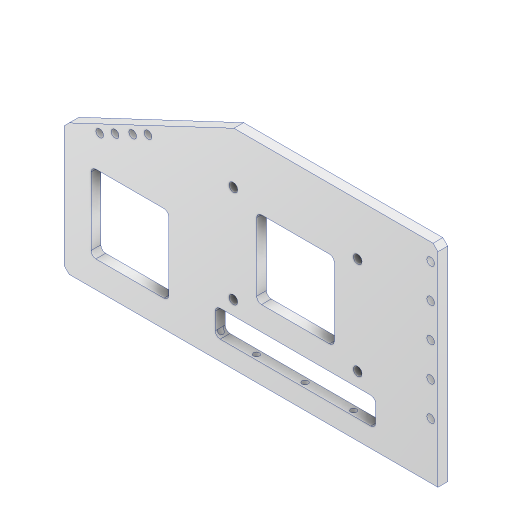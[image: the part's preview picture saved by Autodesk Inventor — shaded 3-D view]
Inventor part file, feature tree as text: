
AUTODESK INVENTOR PART (.ipt)
format: ipt  version: 2023.2 (Build 272271000, 271)  size: 518,656 bytes
history: native  units: mm
features: extrude x12, sketch x12, projected_geometry x9, fillet x3, other x1, chamfer x1
ambient origin geometry x8: Origin, YZ Plane, XZ Plane, XY Plane, X Axis, Y Axis, Z Axis, Center Point
bodies: Body1 (feature_tree)
feature tree (38):
  other  "솔리드1"
  extrude  "돌출1"  Depth=4.0mm TaperAngle=0.0deg
  extrude  "돌출4"  Depth=75.0mm
  extrude  "돌출5"  Depth=32.0mm
  extrude  "돌출6"  Depth=4.0mm TaperAngle=0.0deg
  extrude  "돌출7"  Depth=4.0mm TaperAngle=0.0deg
  fillet  "모깎기1"  Radius=32.0mm
  extrude  "돌출8"  Depth=4.0mm TaperAngle=0.0deg
  extrude  "돌출9"  Depth=5.5mm
  fillet  "모깎기2"  Radius=6.0mm
  chamfer  "모따기1"  Angle=90.0deg  [1 undecoded]
  extrude  "돌출12"  Depth=36.0mm
  extrude  "돌출13"  Depth=3.2mm
  extrude  "돌출14"  Depth=3.2mm
  extrude  "돌출15"  Depth=3.2mm
  fillet  "모깎기3"  Radius=3.2mm
  extrude  "돌출10"  Depth=7.0mm
  sketch  "스케치1"
  sketch  "스케치3"
  projected_geometry  "투영된 루프1"
  sketch  "스케치6"
  projected_geometry  "투영된 루프3"
  sketch  "스케치9"
  projected_geometry  "투영된 루프4"
  sketch  "스케치10"
  sketch  "스케치11"
  projected_geometry  "투영된 루프5"
  sketch  "스케치12"
  projected_geometry  "투영된 루프6"
  sketch  "스케치13"
  sketch  "스케치15"
  projected_geometry  "투영된 루프8"
  sketch  "스케치16"
  projected_geometry  "투영된 루프9"
  sketch  "스케치17"
  projected_geometry  "투영된 루프10"
  sketch  "스케치18"
  projected_geometry  "투영된 루프11"
note: 1 required parameter value undecoded (feature->parameter linkage not recoverable at this tier; creation-order binding heuristic only, values carry confidence <= 0.55)
